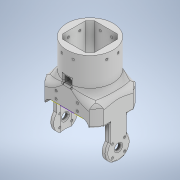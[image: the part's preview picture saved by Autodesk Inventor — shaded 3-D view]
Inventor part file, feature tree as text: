
AUTODESK INVENTOR PART (.ipt)
format: ipt  version: 2021 (Build 250183000, 183)  size: 1,463,808 bytes
history: native  units: mm
features: sketch x21, extrude x19, fillet x14, other x1
ambient origin geometry x8: Origin, YZ Plane, XZ Plane, XY Plane, X Axis, Y Axis, Z Axis, Center Point
bodies: Body1 (feature_tree)
feature tree (55):
  other  "Sólido1"
  extrude  "Extrusión1"  Depth=8.0mm
  extrude  "Extrusión2"  Depth=2.0mm
  fillet  "Empalme1"  Radius=400.0mm
  extrude  "Extrusión3"  Depth=40.0mm TaperAngle=0.0deg
  extrude  "Extrusión4"  Depth=12.0mm TaperAngle=0.0deg
  extrude  "Extrusión5"  Depth=160.0mm TaperAngle=0.0deg
  extrude  "Extrusión7"  Depth=2.0mm
  extrude  "Extrusión8"  Depth=50.0mm TaperAngle=0.0deg
  extrude  "Extrusión9"  Depth=10.0mm
  fillet  "Empalme2"  Radius=10.0mm
  fillet  "Empalme3"  Radius=10.0mm
  extrude  "Extrusión10"  Depth=10.0mm
  extrude  "Extrusión11"  Depth=3.0mm
  fillet  "Empalme4"  Radius=3.0mm
  fillet  "Empalme5"  Radius=500.0mm
  fillet  "Empalme6"  Radius=3.0mm
  fillet  "Empalme7"  Radius=3.0mm
  fillet  "Empalme8"  Radius=500.0mm
  fillet  "Empalme9"  Radius=3.0mm
  fillet  "Empalme10"  Radius=3.0mm
  extrude  "Extrusión12"  Depth=3.0mm
  extrude  "Extrusión13"  Depth=5.0mm
  extrude  "Extrusión14"  Depth=10.0mm
  extrude  "Extrusión15"  Depth=2.0mm
  fillet  "Empalme11"  Radius=0.1mm
  fillet  "Empalme12"  Radius=1.5mm
  extrude  "Extrusión16"  Depth=30.0mm TaperAngle=0.0deg
  extrude  "Extrusión17"  Depth=40.0mm TaperAngle=360.0deg
  extrude  "Extrusión18"  Depth=2.0mm
  fillet  "Empalme14"  Radius=18.0mm
  sketch  "Boceto25"  dims[d108=0.5mm]
  extrude  "Extrusión19"  [1 undecoded]
  fillet  "Empalme15"  [1 undecoded]
  extrude  "Extrusión20"  [1 undecoded]
  sketch  "Boceto28"
  sketch  "Boceto1"  dims[d7=40.0mm d8=0.0mm d10=8.0mm]
  sketch  "Boceto2"  dims[d11=400.0mm d12=0.0mm d13=2.0mm d16=400.0mm d17=0.0mm]
  sketch  "Boceto3"  dims[d18=400.0mm d19=0.0mm d20=40.0mm d21=0.0mm]
  sketch  "Boceto4"  dims[d25=62.249mm d26=0.0mm d27=12.0mm d28=0.0mm]
  sketch  "Boceto5"  dims[d32=9.0mm d37=160.0mm d38=0.0mm]
  sketch  "Boceto8"  dims[d39=2.0mm d40=2.0mm]
  sketch  "Boceto9"  dims[d47=160.0mm d48=0.0mm d49=50.0mm d50=0.0mm]
  sketch  "Boceto13"  dims[d51=10.0mm d52=10.0mm d53=10.0mm d54=10.0mm]
  sketch  "Boceto15"  dims[d55=10.0mm d56=10.0mm]
  sketch  "Boceto16"  dims[d57=10.0mm d62=3.0mm d63=3.0mm d64=500.0mm d65=0.0mm d70=3.0mm d71=3.0mm d72=500.0mm d73=0.0mm d79=3.0mm d80=3.0mm]
  sketch  "Boceto17"  dims[d81=3.0mm d82=3.0mm]
  sketch  "Boceto18"  dims[d83=15.0mm d84=0.0mm d87=5.0mm]
  sketch  "Boceto20"  dims[d88=10.0mm d90=10.0mm]
  sketch  "Boceto21"  dims[d91=15.0mm d92=0.0mm d93=2.0mm d94=0.1mm d95=1.5mm d96=0.0mm]
  sketch  "Boceto22"  dims[d106=100.0mm d107=0.0mm d109=30.0mm d110=0.0mm]
  sketch  "Boceto23"  dims[d111=2.0mm d114=40.0mm d116=360.0deg]
  sketch  "Boceto24"  dims[d118=1000.0mm d119=0.0mm d120=2.0mm d121=18.0mm d122=0.0mm]
  sketch  "Boceto26"
  sketch  "Boceto27"
note: 3 required parameter values undecoded (feature->parameter linkage not recoverable at this tier; creation-order binding heuristic only, values carry confidence <= 0.55)
